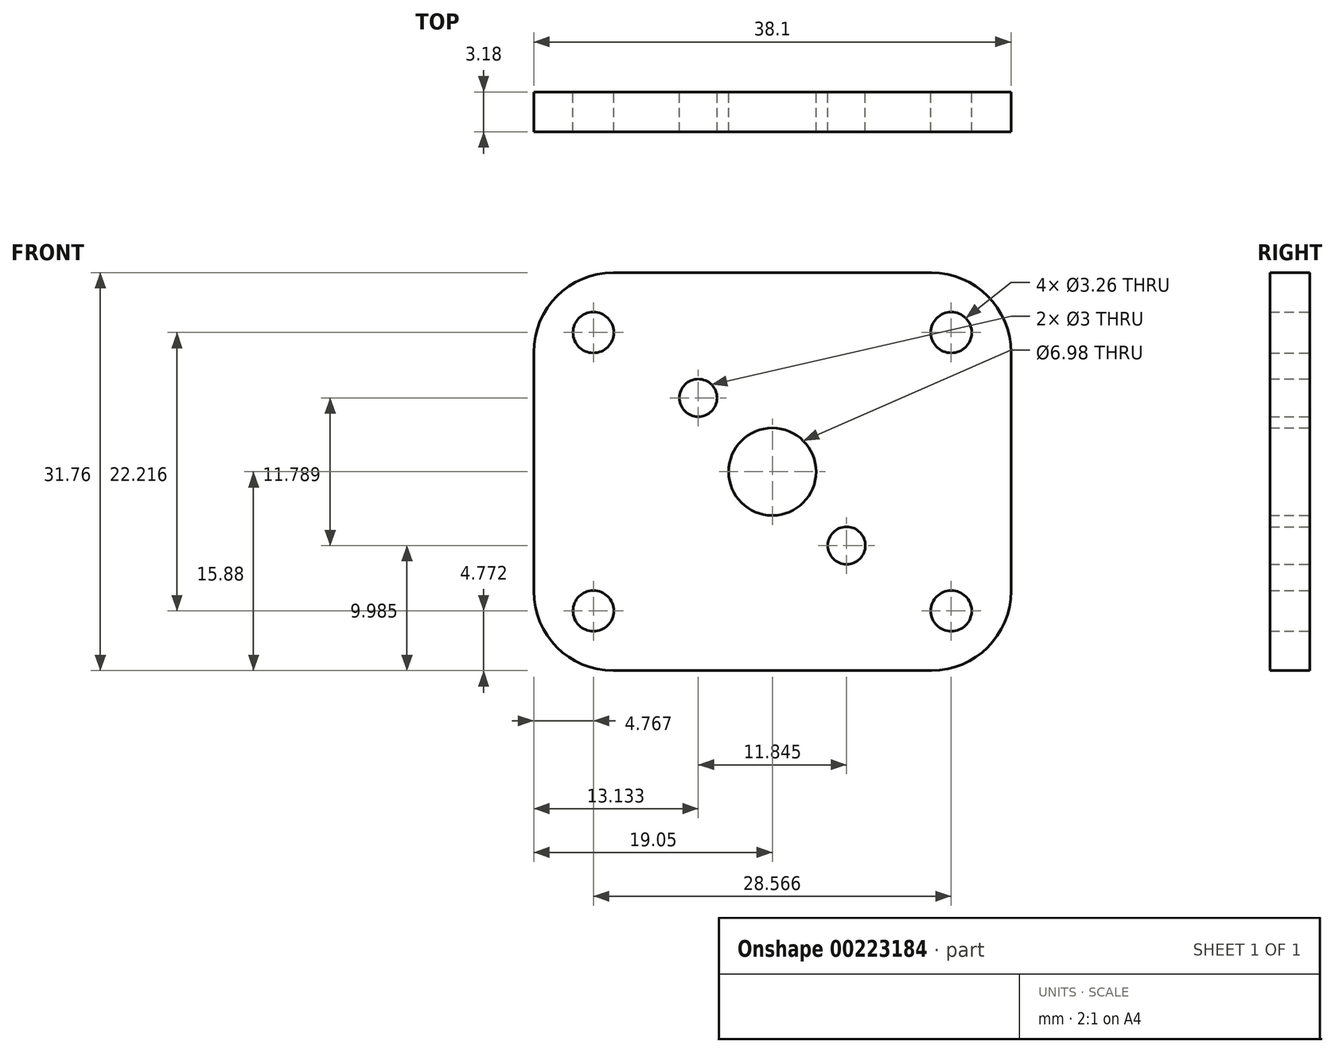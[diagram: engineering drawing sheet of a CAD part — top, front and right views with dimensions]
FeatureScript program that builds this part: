
annotation { "Feature Type Name" : "Feature", "Feature Type Description" : "" }
export const myFeature = defineFeature(function(context is Context, id is Id, definition is map)
    precondition{}
    {
        {
            var Q0;
            Q0=qCreatedBy(makeId("Front.planeOp"),FACE);
            var sketch = newSketch(context, id + "F0", { "sketchPlane" : qUnion([Q0])});
            skLineSegment(sketch, "E0.bottom", {"start": v(12.7, 15.88) * mm, "end": v(-12.7, 15.88) * mm});
            skLineSegment(sketch, "E0.top", {"start": v(12.7, -15.88) * mm, "end": v(-12.7, -15.88) * mm});
            skLineSegment(sketch, "E0.left", {"start": v(19.05, 9.52) * mm, "end": v(19.05, -9.52) * mm});
            skLineSegment(sketch, "E0.right", {"start": v(-19.05, 9.52) * mm, "end": v(-19.05, -9.52) * mm});
            skPoint(sketch, "E1.visualSharp", {"position": v(-19.05, 15.88) * mm});
            skArc(sketch, "E1.filletArc", {"start": v(-12.7, 15.88) * mm, "mid": v(-17.2, 14.02) * mm, "end": v(-19.05, 9.52) * mm});
            skPoint(sketch, "E2.visualSharp", {"position": v(19.05, 15.88) * mm});
            skArc(sketch, "E2.filletArc", {"start": v(19.05, 9.53) * mm, "mid": v(17.2, 14.02) * mm, "end": v(12.7, 15.88) * mm});
            skPoint(sketch, "E3.visualSharp", {"position": v(19.05, -15.87) * mm});
            skArc(sketch, "E3.filletArc", {"start": v(12.7, -15.88) * mm, "mid": v(17.2, -14.02) * mm, "end": v(19.05, -9.52) * mm});
            skPoint(sketch, "E4.visualSharp", {"position": v(-19.05, -15.88) * mm});
            skArc(sketch, "E4.filletArc", {"start": v(-19.05, -9.53) * mm, "mid": v(-17.2, -14.02) * mm, "end": v(-12.7, -15.88) * mm});
            skCircle(sketch, "E5", {"center": v(-14.28, 11.1) * mm, "radius": 1.63 * mm});
            skCircle(sketch, "E6", {"center": v(14.28, 11.1) * mm, "radius": 1.63 * mm});
            skCircle(sketch, "E7", {"center": v(14.28, -11.1) * mm, "radius": 1.63 * mm});
            skCircle(sketch, "E8", {"center": v(-14.28, -11.1) * mm, "radius": 1.63 * mm});
            skCircle(sketch, "E9", {"center": v(-5.92, 5.9) * mm, "radius": 1.5 * mm});
            skCircle(sketch, "E10", {"center": v(5.93, -5.9) * mm, "radius": 1.5 * mm});
            skCircle(sketch, "E11", {"center": v(0, 0) * mm, "radius": 3.49 * mm});
            skSolve(sketch);
        }
        {
            var Q0;
            Q0 = qSketchRegion(id + "F0", true);
            extrude(context, id + "F1", {"entities" : qUnion([Q0]), "depth" : 3.17 * mm});
        }
    });
